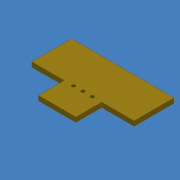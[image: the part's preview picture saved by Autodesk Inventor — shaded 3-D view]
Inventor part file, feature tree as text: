
AUTODESK INVENTOR PART (.ipt)
format: ipt  version: 2012 (Build 160160000, 160)  size: 96,768 bytes
history: native  units: mm (DEFAULTED — no unit token found)
features: sketch x2, extrude x1, hole x1
ambient origin geometry x8: Origin, YZ Plane, XZ Plane, XY Plane, X Axis, Y Axis, Z Axis, Center Point
bodies: Solid1 (feature_tree)
feature tree (4):
  extrude  "Extrusion1"  Depth=10.8mm
  hole  "Hole1"  [1 undecoded]
  sketch  "Sketch1"  dims[d0=27.75mm d1=10.8mm]
  sketch  "Sketch2"  dims[d2=10.15mm d3=7.0mm d4=1.3mm d5=0.0mm d6=2.54mm d7=2.54mm d8=1.0mm d9=6.0mm d10=4.0mm d11=2.0mm d12=14.3117mm d13=8.0mm d14=20.594885mm]
note: 1 required parameter value undecoded (feature->parameter linkage not recoverable at this tier; creation-order binding heuristic only, values carry confidence <= 0.55)
